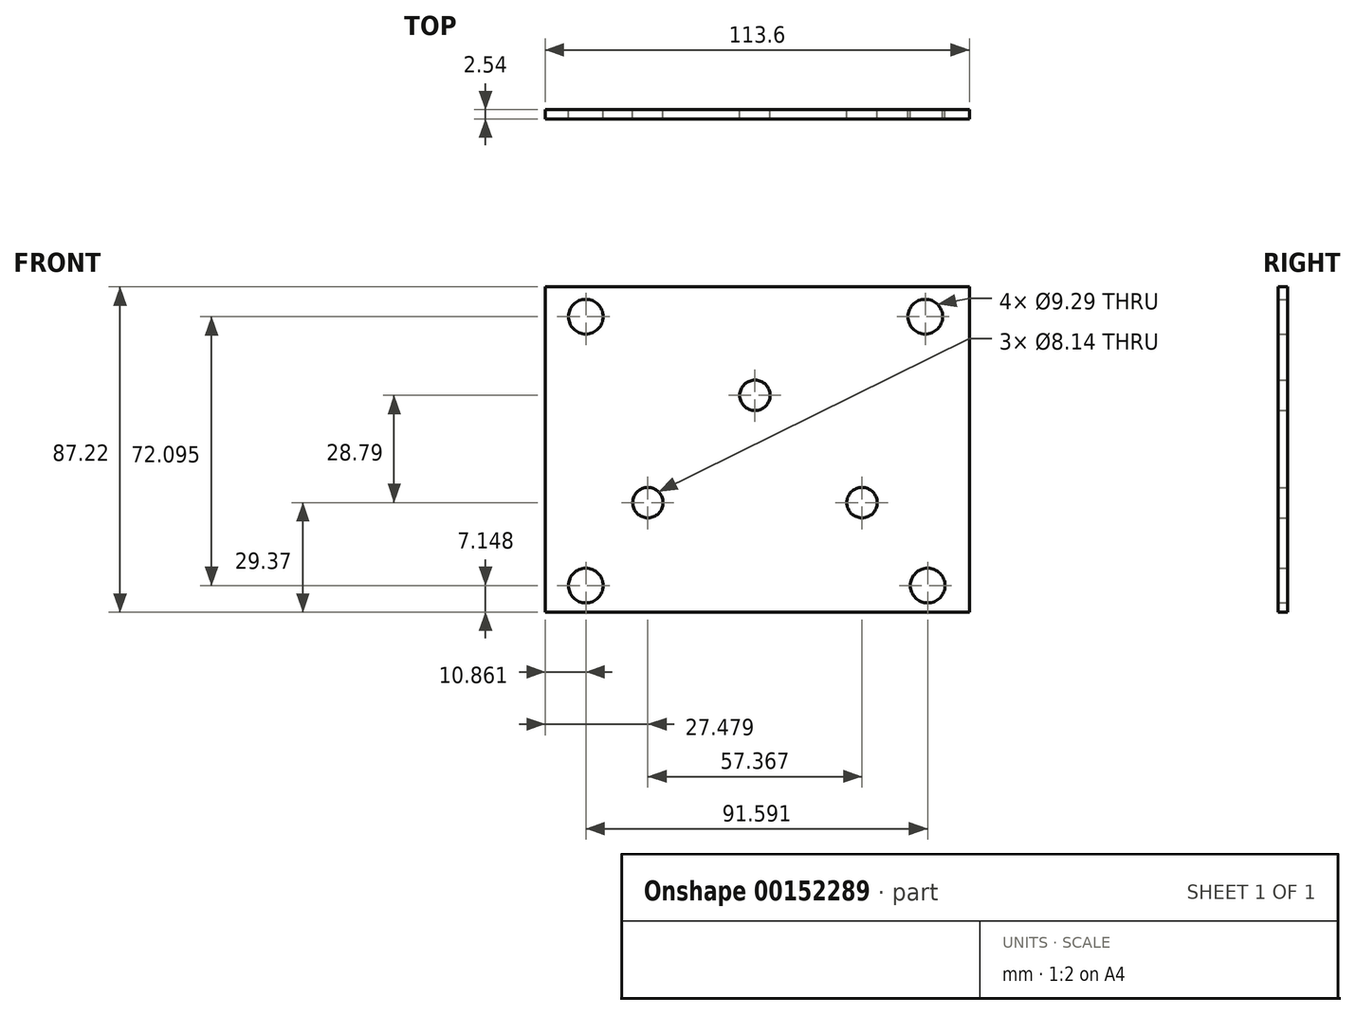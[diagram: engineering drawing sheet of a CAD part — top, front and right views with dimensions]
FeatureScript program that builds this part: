
annotation { "Feature Type Name" : "Feature", "Feature Type Description" : "" }
export const myFeature = defineFeature(function(context is Context, id is Id, definition is map)
    precondition{}
    {
        {
            var Q0;
            Q0=qCreatedBy(makeId("Front.planeOp"),FACE);
            var sketch = newSketch(context, id + "F0", { "sketchPlane" : qUnion([Q0])});
            skLineSegment(sketch, "E0.bottom", {"start": v(60.75, 42.8) * mm, "end": v(-52.85, 42.8) * mm});
            skLineSegment(sketch, "E0.top", {"start": v(60.75, -44.42) * mm, "end": v(-52.85, -44.42) * mm});
            skLineSegment(sketch, "E0.left", {"start": v(60.75, 42.8) * mm, "end": v(60.75, -44.42) * mm});
            skLineSegment(sketch, "E0.right", {"start": v(-52.85, 42.8) * mm, "end": v(-52.85, -44.42) * mm});
            skCircle(sketch, "E1", {"center": v(48.96, 34.82) * mm, "radius": 4.65 * mm});
            skCircle(sketch, "E2", {"center": v(-41.99, 34.82) * mm, "radius": 4.65 * mm});
            skCircle(sketch, "E3", {"center": v(-41.99, -37.27) * mm, "radius": 4.65 * mm});
            skCircle(sketch, "E4", {"center": v(49.6, -37.27) * mm, "radius": 4.65 * mm});
            skCircle(sketch, "E5", {"center": v(3.31, 13.74) * mm, "radius": 4.07 * mm});
            skCircle(sketch, "E6", {"center": v(32, -15.05) * mm, "radius": 4.07 * mm});
            skCircle(sketch, "E7", {"center": v(-25.37, -15.05) * mm, "radius": 4.07 * mm});
            skSolve(sketch);
        }
        {
            var Q0;
            Q0 = qSketchRegion(id + "F0", true);
            extrude(context, id + "F1", {"entities" : qUnion([Q0]), "depth" : 2.54 * mm});
        }
    });
